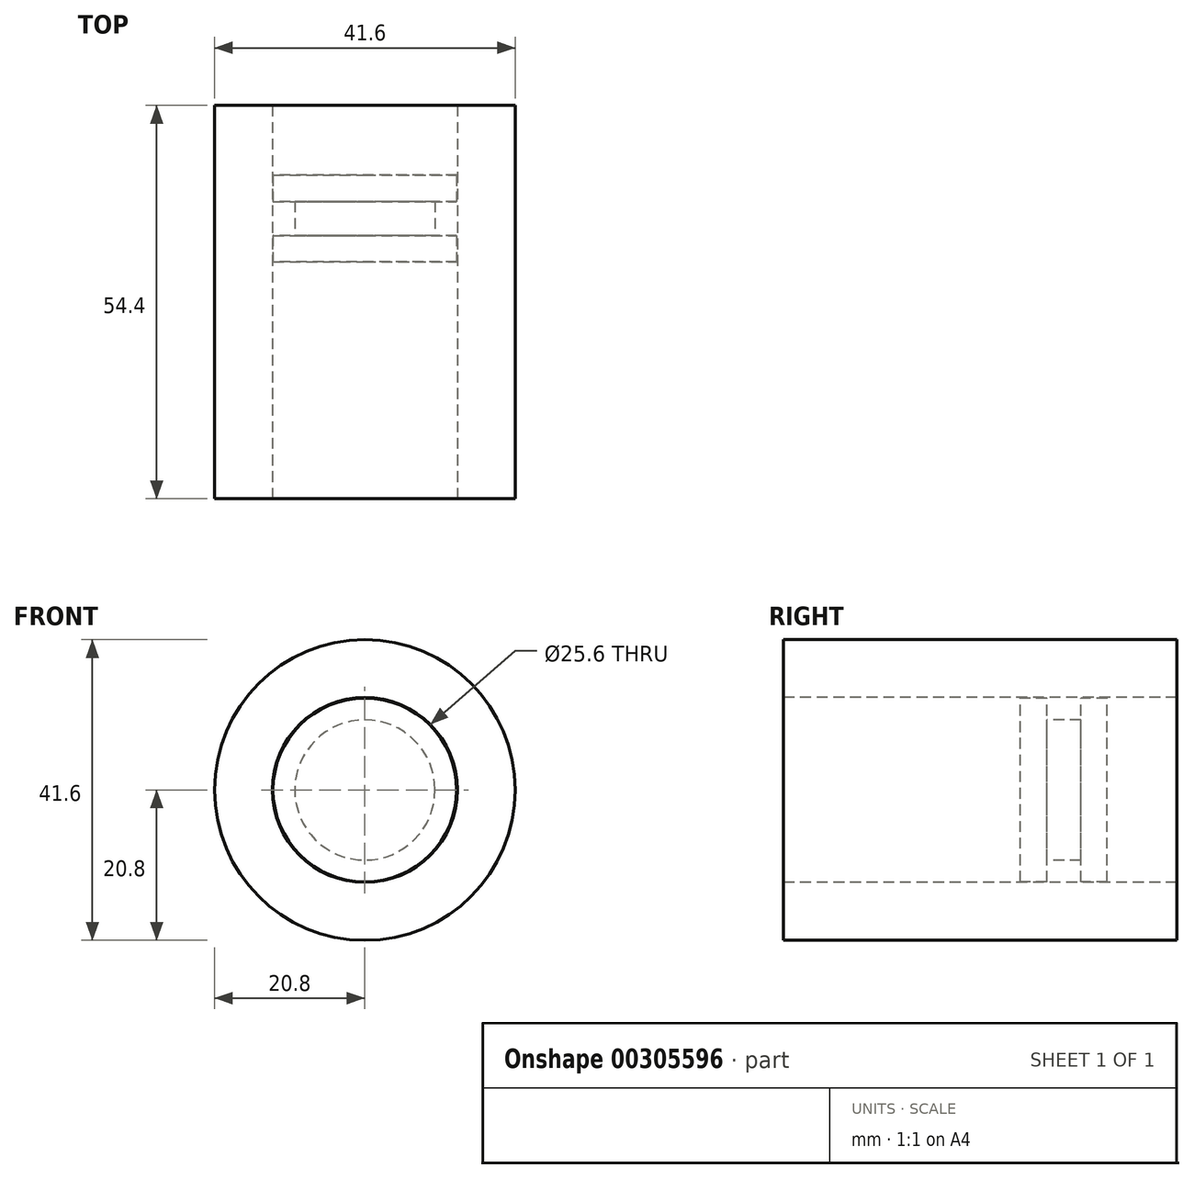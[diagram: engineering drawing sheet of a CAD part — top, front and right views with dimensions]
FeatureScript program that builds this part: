
annotation { "Feature Type Name" : "Feature", "Feature Type Description" : "" }
export const myFeature = defineFeature(function(context is Context, id is Id, definition is map)
    precondition{}
    {
        {
            var Q0;
            Q0=qCreatedBy(makeId("Right.planeOp"),FACE);
            var sketch = newSketch(context, id + "F0", { "sketchPlane" : qUnion([Q0])});
            skLineSegment(sketch, "E0", {"start": v(0, 0) * mm, "end": v(47.46, 0) * mm, "construction": true});
            skLineSegment(sketch, "E1.bottom", {"start": v(0, 20.8) * mm, "end": v(54.4, 20.8) * mm});
            skLineSegment(sketch, "E1.top", {"start": v(0, 12.8) * mm, "end": v(54.4, 12.8) * mm});
            skLineSegment(sketch, "E1.left", {"start": v(0, 20.8) * mm, "end": v(0, 12.8) * mm});
            skLineSegment(sketch, "E1.right", {"start": v(54.4, 20.8) * mm, "end": v(54.4, 12.8) * mm});
            skLineSegment(sketch, "E2", {"start": v(32.77, 0) * mm, "end": v(32.77, 12.7) * mm});
            skLineSegment(sketch, "E3", {"start": v(32.77, 12.7) * mm, "end": v(36.42, 12.7) * mm});
            skLineSegment(sketch, "E4", {"start": v(36.42, 12.7) * mm, "end": v(36.42, 9.7) * mm});
            skLineSegment(sketch, "E5", {"start": v(36.42, 9.7) * mm, "end": v(41.12, 9.7) * mm});
            skLineSegment(sketch, "E6", {"start": v(41.12, 9.7) * mm, "end": v(41.12, 12.7) * mm});
            skLineSegment(sketch, "E7", {"start": v(41.12, 12.7) * mm, "end": v(44.77, 12.7) * mm});
            skLineSegment(sketch, "E8", {"start": v(44.77, 12.7) * mm, "end": v(44.77, 0) * mm});
            skLineSegment(sketch, "E9", {"start": v(44.77, 0) * mm, "end": v(32.77, 0) * mm});
            skLineSegment(sketch, "E10", {"start": v(38.77, 9.7) * mm, "end": v(38.77, 3.42) * mm, "construction": true});
            skCircle(sketch, "E11", {"center": v(38.77, 11.25) * mm, "radius": 1.77 * mm, "construction": true});
            skLineSegment(sketch, "E12", {"start": v(37.62, 11.25) * mm, "end": v(40.08, 11.25) * mm, "construction": true});
            skSolve(sketch);
        }
        {
            var Q0;
            Q0=makeQuery(id+"F0.imprint","IMPRINT",FACE,{"disambiguationData":[TD([[makeQuery(id+"F0.imprint","IMPRINT",EDGE,{"derivedFrom":sQuery(id+"F0.wireOp",EDGE,"E2")}),-1.0]])]});
            var Q1;
            Q1=sQuery(id+"F0.wireOp",EDGE,"E11");
            var Q2;
            Q2=sQuery(id+"F0.wireOp",EDGE,"E0");
            revolve(context, id + "F1", {"surfaceOperationType" : NewSurfaceOperationType.NEW, "entities" : qUnion([Q0]), "surfaceEntities" : qUnion([Q1]), "axis" : qUnion([Q2]), "revolveType" : RevolveType.FULL});
        }
        {
            var Q0;
            Q0=makeQuery(id+"F0.imprint","IMPRINT",FACE,{"disambiguationData":[TD([[makeQuery(id+"F0.imprint","IMPRINT",EDGE,{"derivedFrom":sQuery(id+"F0.wireOp",EDGE,"E1.bottom")}),-1.0]])]});
            var Q1;
            {var subQ0=sQuery(id+"F0.wireOp",EDGE,"E11");var subQ1=sQuery(id+"F0.wireOp",EDGE,"E1.top");var subQ2=makeQuery(id+"F0.imprint","INTERSECT",VERTEX,{"disambiguationData":[OD(0.0)],"derivedFrom":[subQ1,subQ0]});Q1=makeQuery(id+"F0.imprint","IMPRINT",FACE,{"disambiguationData":[TD([[makeQuery(id+"F0.imprint","IMPRINT",EDGE,{"disambiguationData":[TD([[subQ2,-1.0]])],"derivedFrom":subQ1}),1.0]])]});}
            var Q2;
            Q2=sQuery(id+"F0.wireOp",EDGE,"E0");
            revolve(context, id + "F2", {"surfaceOperationType" : NewSurfaceOperationType.NEW, "entities" : qUnion([Q0, Q1]), "axis" : qUnion([Q2]), "revolveType" : RevolveType.FULL});
        }
    });
